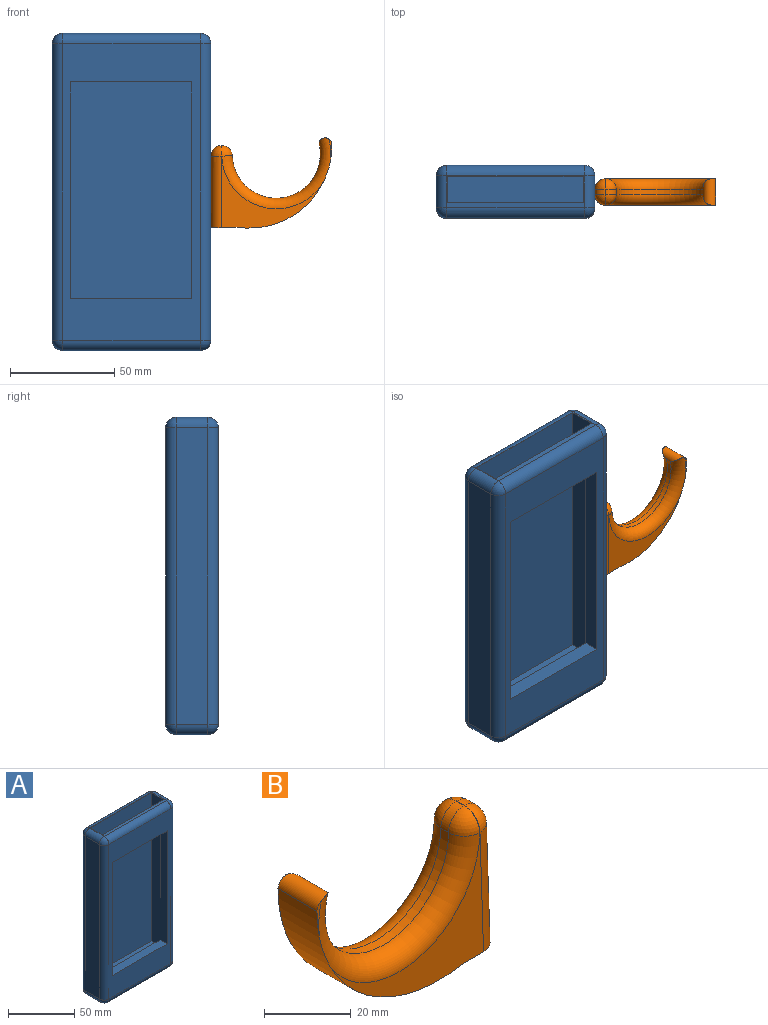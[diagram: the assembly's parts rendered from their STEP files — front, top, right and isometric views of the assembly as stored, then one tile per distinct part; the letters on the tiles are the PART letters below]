
ASSEMBLY  parts=2 mates=1
PART A: 35 faces, bbox 76.2x25.4x152.4 mm
  f0: plane 142.24x66.04mm, normal (0,-1,0), area 3309.7mm2, adj f14,f15,f24,f25,f31,f32,f33,f34
  f1: plane 136.53x65.02mm, normal (0,1,0), area 2793.5mm2, adj f5,f7,f8,f10,f31,f32,f33,f34
  f2: plane 142.24x15.24mm, normal (-1,0,0), area 2167.7mm2, adj f19,f24,f27,f30
  f3: plane 66.04x15.24mm, normal (0,0,-1), area 1006.4mm2, adj f16,f25,f26,f30
  f4: plane 142.24x15.24mm, normal (1,0,0), area 2167.7mm2, adj f11,f15,f16,f17
  f5: plane 66.04x15.24mm, normal (0,0,1), area 180.6mm2, adj f1,f7,f8,f9,f11,f14,f18,f19
  f6: plane 142.24x66.04mm, normal (0,1,0), area 9393.5mm2, adj f17,f18,f26,f27
  f7: plane 136.53x12.7mm, normal (1,0,0), area 1733.9mm2, adj f1,f5,f9,f10
  f8: plane 136.53x12.7mm, normal (-1,0,0), area 1733.9mm2, adj f1,f5,f9,f10
  f9: plane 136.53x65.02mm, normal (0,-1,0), area 8877.4mm2, adj f5,f7,f8,f10
  f10: plane 65.02x12.7mm, normal (0,0,1), area 825.8mm2, adj f1,f7,f8,f9
  f11: cylinder r=5.08mm len=15.24mm, axis (0,1,0), area 121.6mm2, adj f4,f5,f12,f13
  f12: sphere r=5.08mm, area 40.5mm2, adj f11,f14,f15
  f13: sphere r=5.08mm, area 40.5mm2, adj f11,f17,f18
  f14: cylinder r=5.08mm len=66.04mm, axis (1,0,0), area 527mm2, adj f0,f5,f12,f20
  f15: cylinder r=5.08mm len=142.24mm, axis (0,0,-1), area 1135mm2, adj f0,f4,f12,f21
  f16: cylinder r=5.08mm len=15.24mm, axis (0,-1,0), area 121.6mm2, adj f3,f4,f21,f22
  f17: cylinder r=5.08mm len=142.24mm, axis (0,0,1), area 1135mm2, adj f4,f6,f13,f22
  f18: cylinder r=5.08mm len=66.04mm, axis (-1,0,0), area 527mm2, adj f5,f6,f13,f23
  f19: cylinder r=5.08mm len=15.24mm, axis (0,-1,0), area 121.6mm2, adj f2,f5,f20,f23
  f20: sphere r=5.08mm, area 40.5mm2, adj f14,f19,f24
  f21: sphere r=5.08mm, area 40.5mm2, adj f15,f16,f25
  f22: sphere r=5.08mm, area 40.5mm2, adj f16,f17,f26
  f23: sphere r=5.08mm, area 40.5mm2, adj f18,f19,f27
  f24: cylinder r=5.08mm len=142.24mm, axis (0,0,1), area 1135mm2, adj f0,f2,f20,f28
  f25: cylinder r=5.08mm len=66.04mm, axis (-1,0,0), area 527mm2, adj f0,f3,f21,f28
  f26: cylinder r=5.08mm len=66.04mm, axis (1,0,0), area 527mm2, adj f3,f6,f22,f29
  f27: cylinder r=5.08mm len=142.24mm, axis (0,0,-1), area 1135mm2, adj f2,f6,f23,f29
  f28: sphere r=5.08mm, area 40.5mm2, adj f24,f25,f30
  f29: sphere r=5.08mm, area 40.5mm2, adj f26,f27,f30
  f30: cylinder r=5.08mm len=15.24mm, axis (0,1,0), area 121.6mm2, adj f2,f3,f28,f29
  f31: plane 104.14x7.45mm, normal (1,0,0), area 775.9mm2, adj f0,f1,f32,f34
  f32: plane 58.42x7.45mm, normal (0,0,1), area 435.2mm2, adj f0,f1,f31,f33
  f33: plane 104.14x7.45mm, normal (-1,0,0), area 775.9mm2, adj f0,f1,f32,f34
  f34: plane 58.42x7.45mm, normal (0,0,-1), area 435.2mm2, adj f0,f1,f31,f33
PART B: 22 faces, bbox 64.9x12.8x44.5 mm
  f0: plane 10.29x1.43mm, normal (0,-1,0), area 4.8mm2, adj f6,f7,f10
  f1: plane 10.29x1.43mm, normal (0,1,0), area 4.8mm2, adj f6,f7,f12
  f2: plane 12.77x12.1mm, normal (0,0,-1), area 141.7mm2, adj f3,f7,f8,f9,f15,f18
  f3: plane 34.43x2.54mm, normal (1,0,0.03), area 87.5mm2, adj f2,f15,f18,f21
  f4: plane 2.54x0.09mm, normal (0,0,1), area 0.2mm2, adj f11,f16,f17,f21
  f5: cylinder r=21.15mm len=42.3mm, axis (0,1,0), area 179.6mm2, adj f6,f10,f11,f12
  f6: cylinder r=3.07mm len=12.7mm, axis (0,1,0), area 97.7mm2, adj f0,f1,f5,f7,f10,f12
  f7: cylinder r=39.54mm len=47.36mm, axis (0,1,0), area 886.3mm2, adj f0,f1,f2,f6,f8,f9,f10,f12
  f8: plane 50.07x35.04mm, normal (0,-1,0), area 462mm2, adj f2,f7,f10,f15,f16
  f9: plane 50.07x35.04mm, normal (0,1,0), area 462mm2, adj f2,f7,f12,f17,f18
  f10: torus R=26.23mm, axis (0,-1,0), area 623.3mm2, adj f0,f5,f6,f7,f8,f13
  f11: cylinder r=5.08mm len=5.08mm, axis (0,1,0), area 20.3mm2, adj f4,f5,f13,f14
  f12: torus R=26.23mm, axis (0,-1,0), area 623.3mm2, adj f1,f5,f6,f7,f9,f14
  f13: sphere r=5.08mm, area 40.5mm2, adj f10,f11,f16
  f14: sphere r=5.08mm, area 40.5mm2, adj f11,f12,f17
  f15: cylinder r=5.08mm len=34.6mm, axis (0.03,0,-1), area 274.2mm2, adj f2,f3,f8,f19
  f16: cylinder r=5.08mm len=5.08mm, axis (1,0,0), area 0.7mm2, adj f4,f8,f13,f19
  f17: cylinder r=5.08mm len=5.08mm, axis (-1,0,0), area 0.7mm2, adj f4,f9,f14,f20
  f18: cylinder r=5.08mm len=34.6mm, axis (-0.03,0,1), area 274.2mm2, adj f2,f3,f9,f20
  f19: sphere r=5.08mm, area 39.8mm2, adj f15,f16,f21
  f20: sphere r=5.08mm, area 39.8mm2, adj f17,f18,f21
  f21: cylinder r=5.08mm len=5.08mm, axis (0,1,0), area 19.8mm2, adj f3,f4,f19,f20
PLACE A t=(-40.98,-10.23,-0.62)mm
PLACE B rot(axis=(0.02,0,-1),180deg) t=(17.76,-29.28,-3.08)mm
MATE fastened B.f3 <-> A.f4  axis (-1,0,0) through (-0.15,-22.93,-1.27)mm
